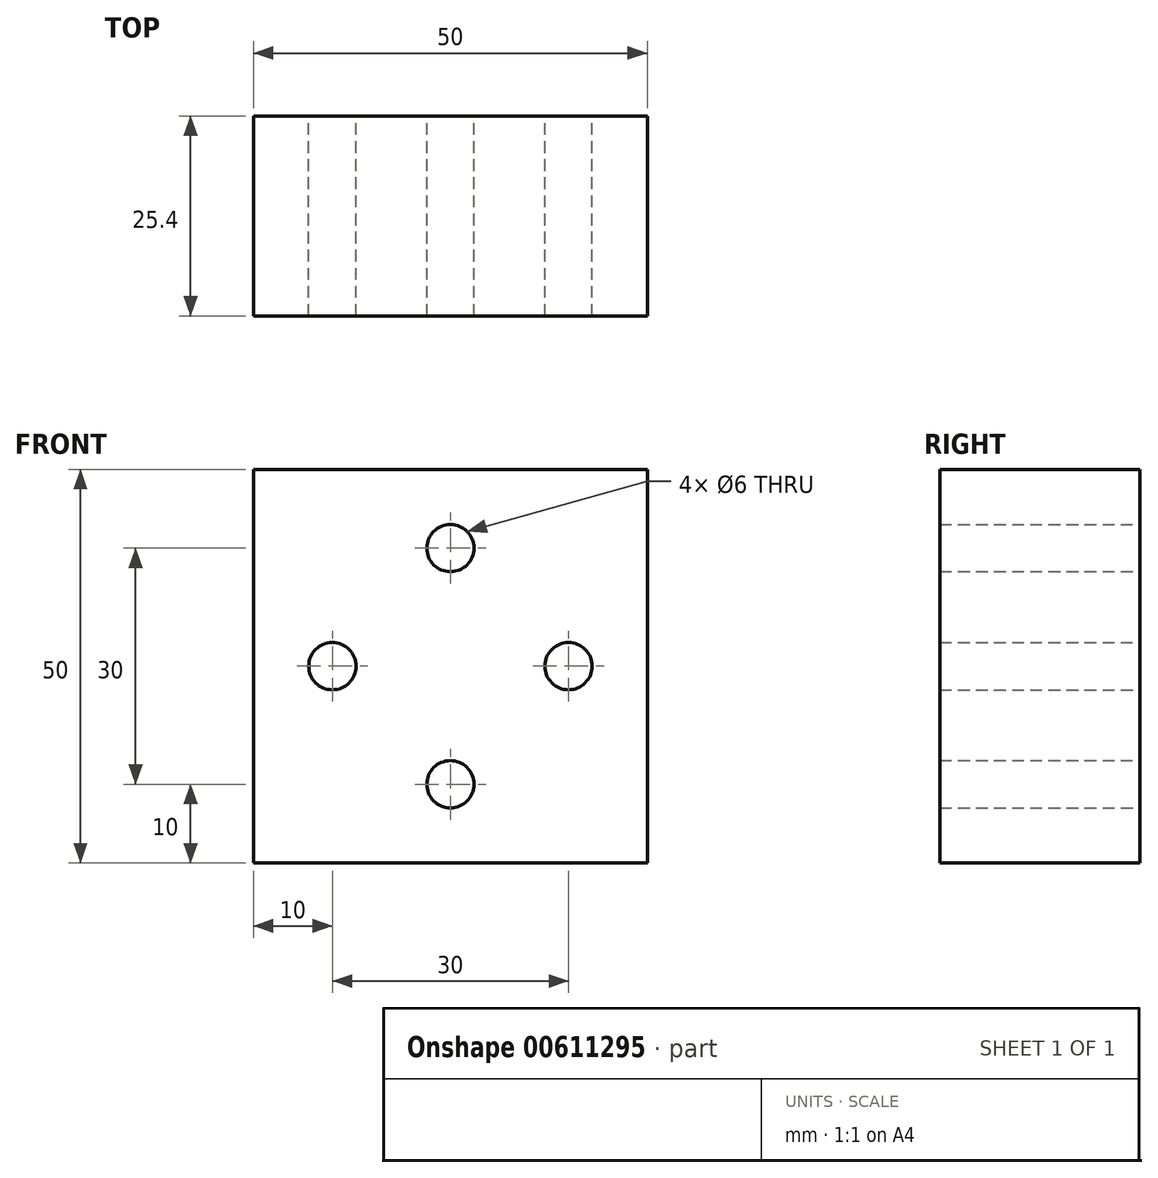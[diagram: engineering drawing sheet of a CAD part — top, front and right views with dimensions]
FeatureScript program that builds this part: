
annotation { "Feature Type Name" : "Feature", "Feature Type Description" : "" }
export const myFeature = defineFeature(function(context is Context, id is Id, definition is map)
    precondition{}
    {
        {
            var Q0;
            Q0=qCreatedBy(makeId("Front.planeOp"),FACE);
            var sketch = newSketch(context, id + "F0", { "sketchPlane" : qUnion([Q0])});
            skLineSegment(sketch, "E0.bottom", {"start": v(25, 25) * mm, "end": v(-25, 25) * mm});
            skLineSegment(sketch, "E0.top", {"start": v(25, -25) * mm, "end": v(-25, -25) * mm});
            skLineSegment(sketch, "E0.left", {"start": v(25, 25) * mm, "end": v(25, -25) * mm});
            skLineSegment(sketch, "E0.right", {"start": v(-25, 25) * mm, "end": v(-25, -25) * mm});
            skPoint(sketch, "E0.middle", {"position": v(0, 0) * mm});
            skLineSegment(sketch, "E1.bottom", {"start": v(15, 15) * mm, "end": v(-15, 15) * mm, "construction": true});
            skLineSegment(sketch, "E1.top", {"start": v(15, -15) * mm, "end": v(-15, -15) * mm, "construction": true});
            skLineSegment(sketch, "E1.left", {"start": v(15, 15) * mm, "end": v(15, -15) * mm, "construction": true});
            skLineSegment(sketch, "E1.right", {"start": v(-15, 15) * mm, "end": v(-15, -15) * mm, "construction": true});
            skLineSegment(sketch, "E2", {"start": v(0, 15) * mm, "end": v(-15, 0) * mm, "construction": true});
            skLineSegment(sketch, "E3", {"start": v(-15, 0) * mm, "end": v(0, -15) * mm, "construction": true});
            skLineSegment(sketch, "E4", {"start": v(0, -15) * mm, "end": v(15, 0) * mm, "construction": true});
            skLineSegment(sketch, "E5", {"start": v(15, 0) * mm, "end": v(0, 15) * mm, "construction": true});
            skCircle(sketch, "E6", {"center": v(0, 15) * mm, "radius": 3 * mm});
            skCircle(sketch, "E7", {"center": v(-15, 0) * mm, "radius": 3 * mm});
            skCircle(sketch, "E8", {"center": v(0, -15) * mm, "radius": 3 * mm});
            skCircle(sketch, "E9", {"center": v(15, 0) * mm, "radius": 3 * mm});
            skLineSegment(sketch, "E10", {"start": v(-19.24, 0) * mm, "end": v(0, 19.24) * mm, "construction": true});
            skLineSegment(sketch, "E11", {"start": v(0, 19.24) * mm, "end": v(19.24, 0) * mm, "construction": true});
            skLineSegment(sketch, "E12", {"start": v(19.24, 0) * mm, "end": v(0, -19.24) * mm, "construction": true});
            skLineSegment(sketch, "E13", {"start": v(0, -19.24) * mm, "end": v(-19.24, 0) * mm, "construction": true});
            skSolve(sketch);
        }
        {
            var Q0;
            Q0=makeQuery(id+"F0.imprint","IMPRINT",FACE,{"disambiguationData":[TD([[makeQuery(id+"F0.imprint","IMPRINT",EDGE,{"derivedFrom":sQuery(id+"F0.wireOp",EDGE,"E0.bottom")}),1.0]])]});
            extrude(context, id + "F1", {"entities" : qUnion([Q0]), "depth" : 25.4 * mm, "offsetDistance" : 25 * mm});
        }
    });
